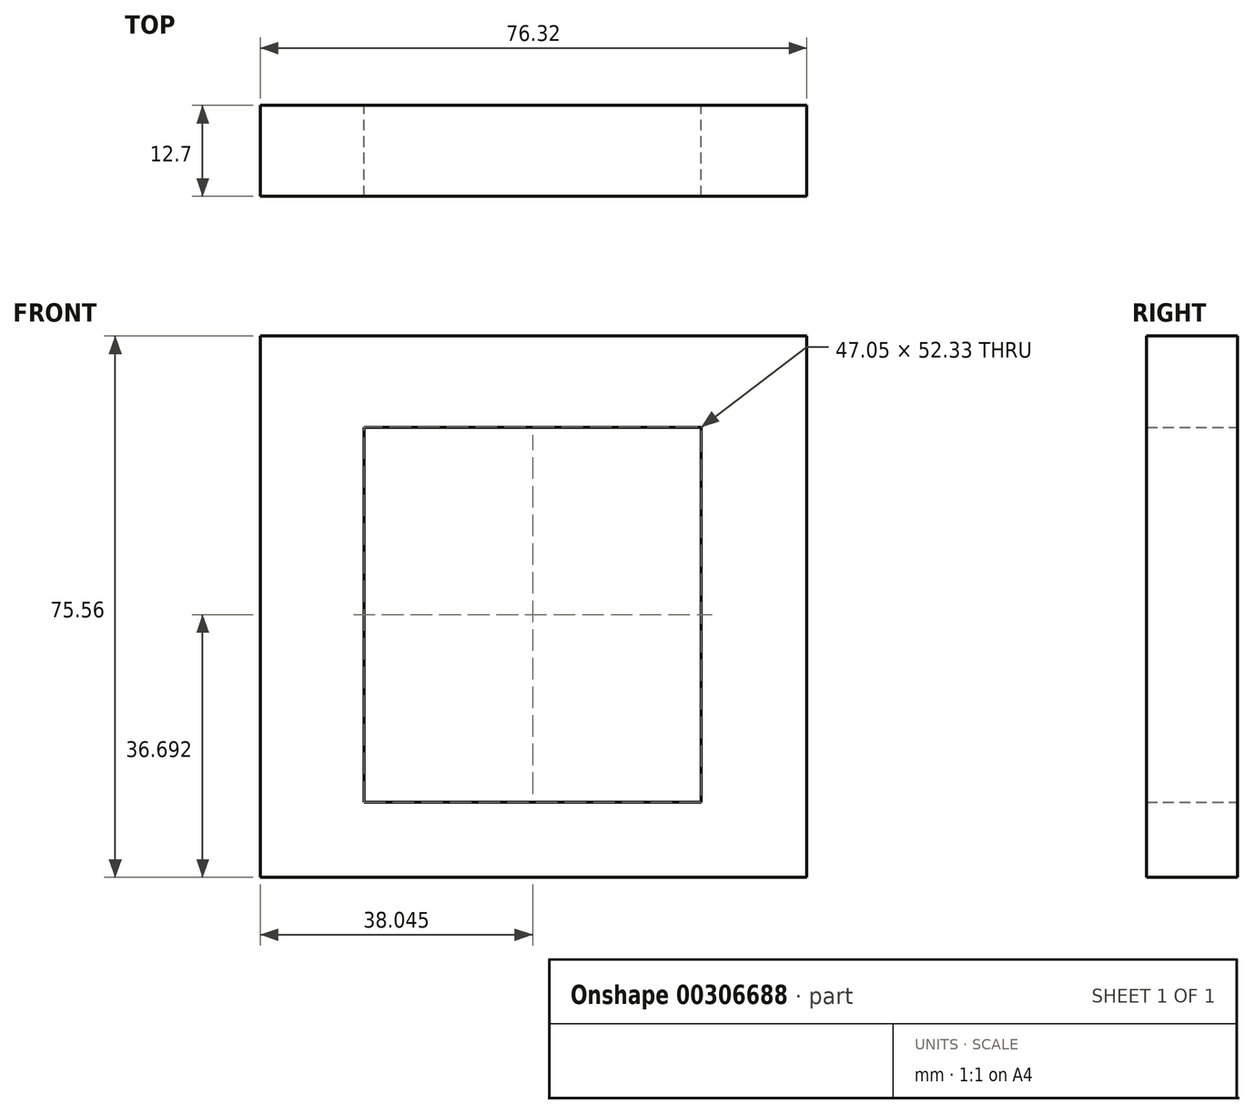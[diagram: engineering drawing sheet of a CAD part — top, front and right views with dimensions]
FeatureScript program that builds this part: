
annotation { "Feature Type Name" : "Feature", "Feature Type Description" : "" }
export const myFeature = defineFeature(function(context is Context, id is Id, definition is map)
    precondition{}
    {
        {
            var Q0;
            Q0=qCreatedBy(makeId("Front.planeOp"),FACE);
            var sketch = newSketch(context, id + "F0", { "sketchPlane" : qUnion([Q0])});
            skLineSegment(sketch, "E0.bottom", {"start": v(0, 0) * mm, "end": v(0, 0) * mm});
            skLineSegment(sketch, "E0.top", {"start": v(0, -75.56) * mm, "end": v(0, -75.56) * mm});
            skLineSegment(sketch, "E0.left", {"start": v(0, 0) * mm, "end": v(0, -75.56) * mm});
            skLineSegment(sketch, "E0.right", {"start": v(0, 0) * mm, "end": v(0, -75.56) * mm});
            skLineSegment(sketch, "E1.bottom", {"start": v(0, -75.56) * mm, "end": v(76.32, -75.56) * mm});
            skLineSegment(sketch, "E1.top", {"start": v(0, 0) * mm, "end": v(76.32, 0) * mm});
            skLineSegment(sketch, "E1.left", {"start": v(0, -75.56) * mm, "end": v(0, 0) * mm});
            skLineSegment(sketch, "E1.right", {"start": v(76.32, -75.56) * mm, "end": v(76.32, 0) * mm});
            skLineSegment(sketch, "E2.bottom", {"start": v(131.63, -74.03) * mm, "end": v(124.56, -74.03) * mm});
            skLineSegment(sketch, "E2.top", {"start": v(131.63, -72.37) * mm, "end": v(124.56, -72.37) * mm});
            skLineSegment(sketch, "E2.left", {"start": v(131.63, -74.03) * mm, "end": v(131.63, -72.37) * mm});
            skLineSegment(sketch, "E2.right", {"start": v(124.56, -74.03) * mm, "end": v(124.56, -72.37) * mm});
            skLineSegment(sketch, "E3.bottom", {"start": v(14.52, -12.7) * mm, "end": v(61.57, -12.7) * mm});
            skLineSegment(sketch, "E3.top", {"start": v(14.52, -65.03) * mm, "end": v(61.57, -65.03) * mm});
            skLineSegment(sketch, "E3.left", {"start": v(14.52, -12.7) * mm, "end": v(14.52, -65.03) * mm});
            skLineSegment(sketch, "E3.right", {"start": v(61.57, -12.7) * mm, "end": v(61.57, -65.03) * mm});
            skLineSegment(sketch, "E4.bottom", {"start": v(0, -12.7) * mm, "end": v(14.52, -12.7) * mm});
            skLineSegment(sketch, "E4.top", {"start": v(0, 0) * mm, "end": v(14.52, 0) * mm});
            skLineSegment(sketch, "E4.left", {"start": v(0, -12.7) * mm, "end": v(0, 0) * mm});
            skLineSegment(sketch, "E4.right", {"start": v(14.52, -12.7) * mm, "end": v(14.52, 0) * mm});
            skLineSegment(sketch, "E5.bottom", {"start": v(61.57, -12.7) * mm, "end": v(76.32, -12.7) * mm});
            skLineSegment(sketch, "E5.top", {"start": v(61.57, 0) * mm, "end": v(76.32, 0) * mm});
            skLineSegment(sketch, "E5.left", {"start": v(61.57, -12.7) * mm, "end": v(61.57, 0) * mm});
            skLineSegment(sketch, "E5.right", {"start": v(76.32, -12.7) * mm, "end": v(76.32, 0) * mm});
            skSolve(sketch);
        }
        {
            var Q0;
            Q0=makeQuery(id+"F0.imprint","IMPRINT",FACE,{"disambiguationData":[TD([[makeQuery(id+"F0.imprint","IMPRINT",EDGE,{"derivedFrom":sQuery(id+"F0.wireOp",EDGE,"E1.bottom")}),1.0]])]});
            var Q1;
            Q1=makeQuery(id+"F0.imprint","IMPRINT",FACE,{"disambiguationData":[TD([[makeQuery(id+"F0.imprint","IMPRINT",EDGE,{"derivedFrom":sQuery(id+"F0.wireOp",EDGE,"E1.top")}),-1.0]])]});
            extrude(context, id + "F1", {"entities" : qUnion([Q0, Q1]), "depth" : 12.7 * mm});
        }
    });
